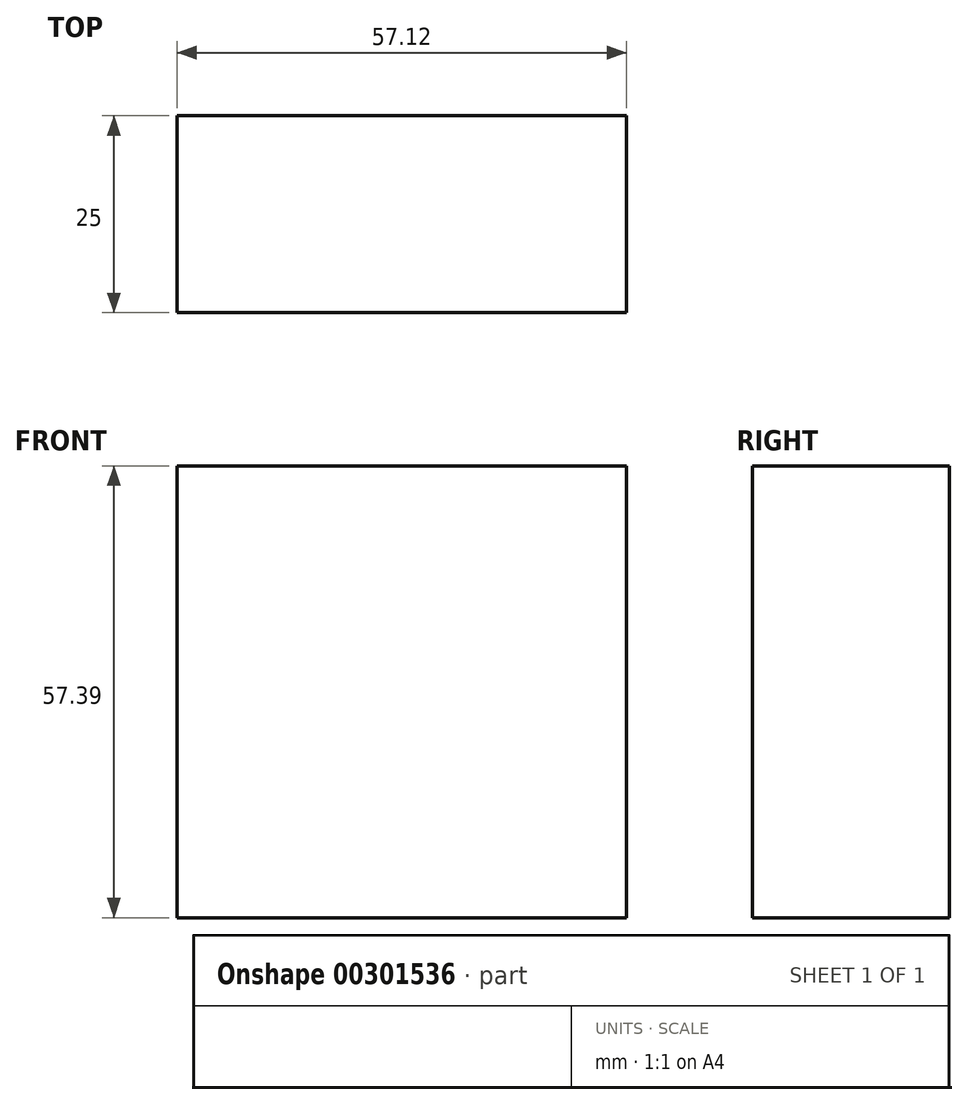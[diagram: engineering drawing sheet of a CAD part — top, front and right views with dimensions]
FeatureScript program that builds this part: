
annotation { "Feature Type Name" : "Feature", "Feature Type Description" : "" }
export const myFeature = defineFeature(function(context is Context, id is Id, definition is map)
    precondition{}
    {
        {
            var Q0;
            Q0=qCreatedBy(makeId("Front.planeOp"),FACE);
            var sketch = newSketch(context, id + "F0", { "sketchPlane" : qUnion([Q0])});
            skLineSegment(sketch, "E0.bottom", {"start": v(-84.7, 20.98) * mm, "end": v(-27.59, 20.98) * mm});
            skLineSegment(sketch, "E0.top", {"start": v(-84.7, 78.37) * mm, "end": v(-27.59, 78.37) * mm});
            skLineSegment(sketch, "E0.left", {"start": v(-84.7, 20.98) * mm, "end": v(-84.7, 78.37) * mm});
            skLineSegment(sketch, "E0.right", {"start": v(-27.59, 20.98) * mm, "end": v(-27.59, 78.37) * mm});
            skPoint(sketch, "E0.middle", {"position": v(-56.15, 49.68) * mm});
            skSolve(sketch);
        }
        {
            var Q0;
            Q0=makeQuery(id+"F0.imprint","IMPRINT",FACE,{"disambiguationData":[TD([[makeQuery(id+"F0.imprint","IMPRINT",EDGE,{"derivedFrom":sQuery(id+"F0.wireOp",EDGE,"E0.bottom")}),1.0]])]});
            extrude(context, id + "F1", {"entities" : qUnion([Q0]), "depth" : 25 * mm});
        }
    });
